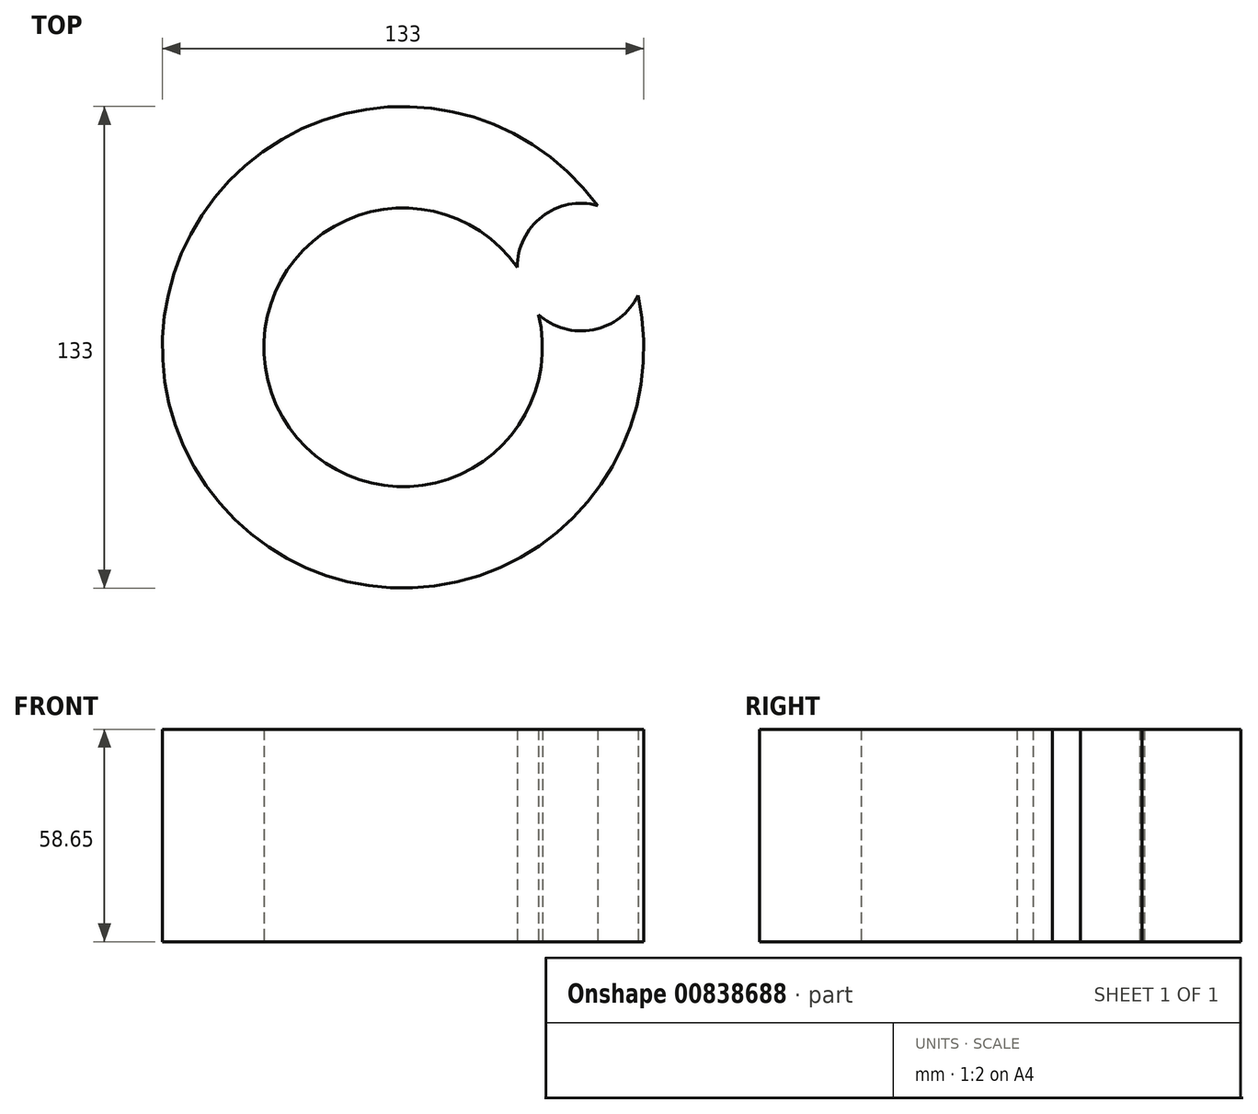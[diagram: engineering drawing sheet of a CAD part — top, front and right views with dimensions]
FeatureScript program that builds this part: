
annotation { "Feature Type Name" : "Feature", "Feature Type Description" : "" }
export const myFeature = defineFeature(function(context is Context, id is Id, definition is map)
    precondition{}
    {
        {
            var Q0;
            Q0=qCreatedBy(makeId("Top.planeOp"),FACE);
            var sketch = newSketch(context, id + "F0", { "sketchPlane" : qUnion([Q0])});
            skCircle(sketch, "E0", {"center": v(0, 0) * mm, "radius": 38.48 * mm});
            skCircle(sketch, "E1", {"center": v(49.15, 22.17) * mm, "radius": 17.62 * mm});
            skCircle(sketch, "E2", {"center": v(0, 0) * mm, "radius": 66.5 * mm});
            skSolve(sketch);
        }
        {
            var Q0;
            {var subQ0=sQuery(id+"F0.wireOp",EDGE,"E1");var subQ1=sQuery(id+"F0.wireOp",EDGE,"E0");var subQ2=makeQuery(id+"F0.imprint","INTERSECT",VERTEX,{"disambiguationData":[OD(0.0)],"derivedFrom":[subQ1,subQ0]});Q0=makeQuery(id+"F0.imprint","IMPRINT",FACE,{"disambiguationData":[TD([[makeQuery(id+"F0.imprint","IMPRINT",EDGE,{"disambiguationData":[TD([[subQ2,-1.0]])],"derivedFrom":subQ1}),-1.0]])]});}
            var Q1;
            Q1=sQuery(id+"F0.wireOp",EDGE,"E0");
            var Q2;
            Q2=sQuery(id+"F0.wireOp",EDGE,"E2");
            extrude(context, id + "F1", {"entities" : qUnion([Q0]), "surfaceEntities" : qUnion([Q1, Q2]), "depth" : 58.65 * mm, "offsetDistance" : 25.4 * mm});
        }
    });
